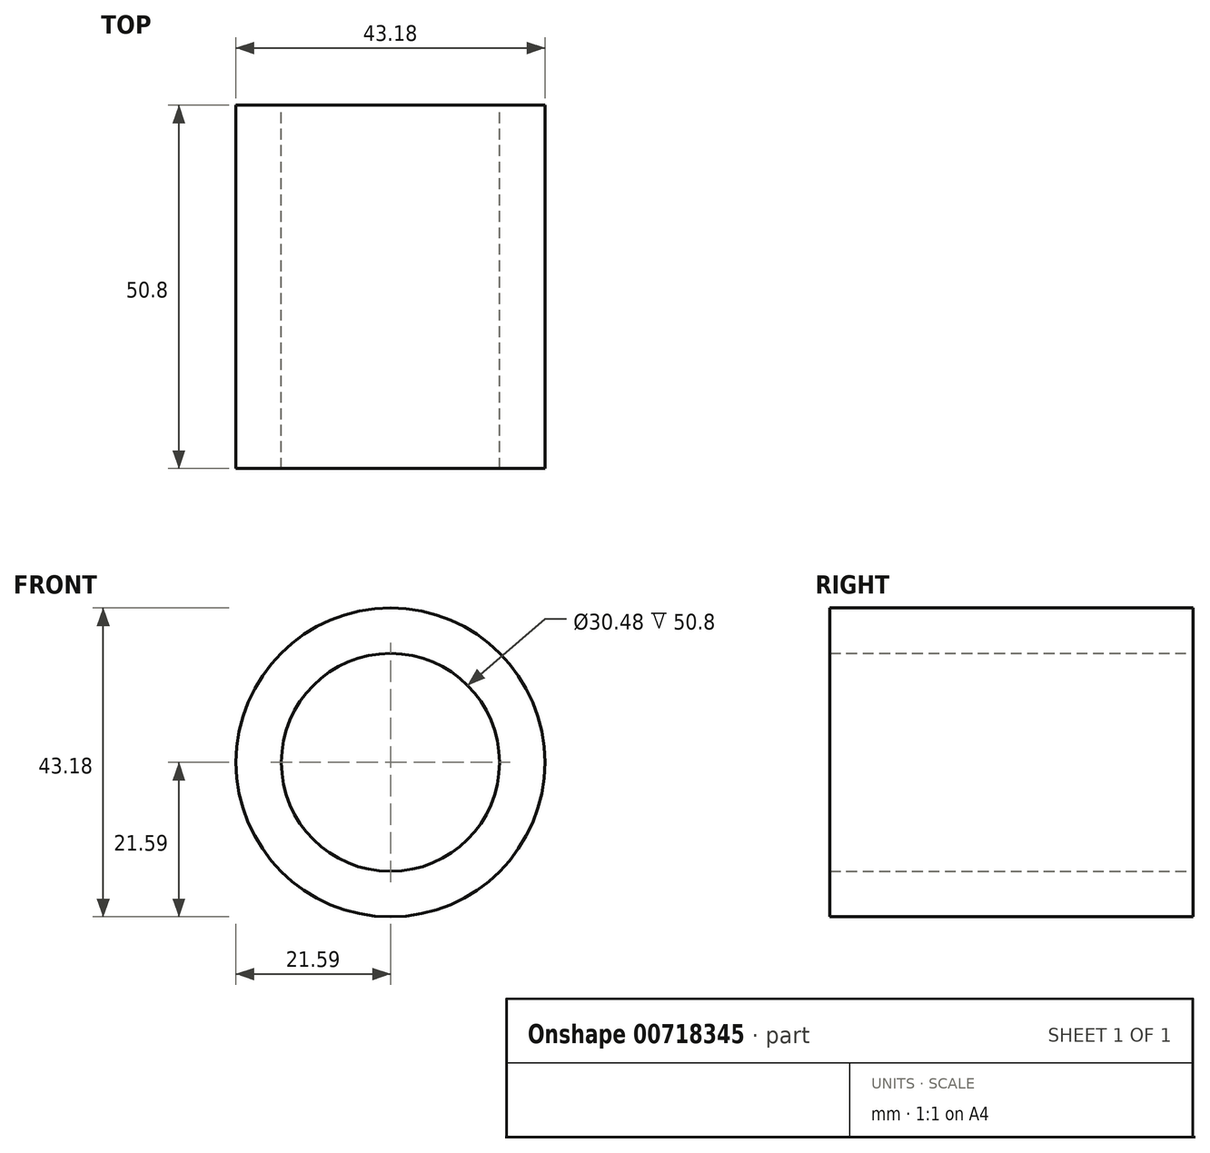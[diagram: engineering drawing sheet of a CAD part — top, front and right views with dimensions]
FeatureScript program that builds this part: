
annotation { "Feature Type Name" : "Feature", "Feature Type Description" : "" }
export const myFeature = defineFeature(function(context is Context, id is Id, definition is map)
    precondition{}
    {
        {
            var Q0;
            Q0=qCreatedBy(makeId("Front.planeOp"),FACE);
            var sketch = newSketch(context, id + "F0", { "sketchPlane" : qUnion([Q0])});
            skCircle(sketch, "E0", {"center": v(0, 0) * mm, "radius": 21.59 * mm});
            skCircle(sketch, "E1", {"center": v(0, 0) * mm, "radius": 15.24 * mm});
            skSolve(sketch);
        }
        {
            var Q0;
            Q0=makeQuery(id+"F0.imprint","IMPRINT",FACE,{"disambiguationData":[TD([[makeQuery(id+"F0.imprint","IMPRINT",EDGE,{"derivedFrom":sQuery(id+"F0.wireOp",EDGE,"E0")}),1.0]])]});
            extrude(context, id + "F1", {"entities" : qUnion([Q0]), "depth" : 50.8 * mm, "offsetDistance" : 25.4 * mm});
        }
    });
